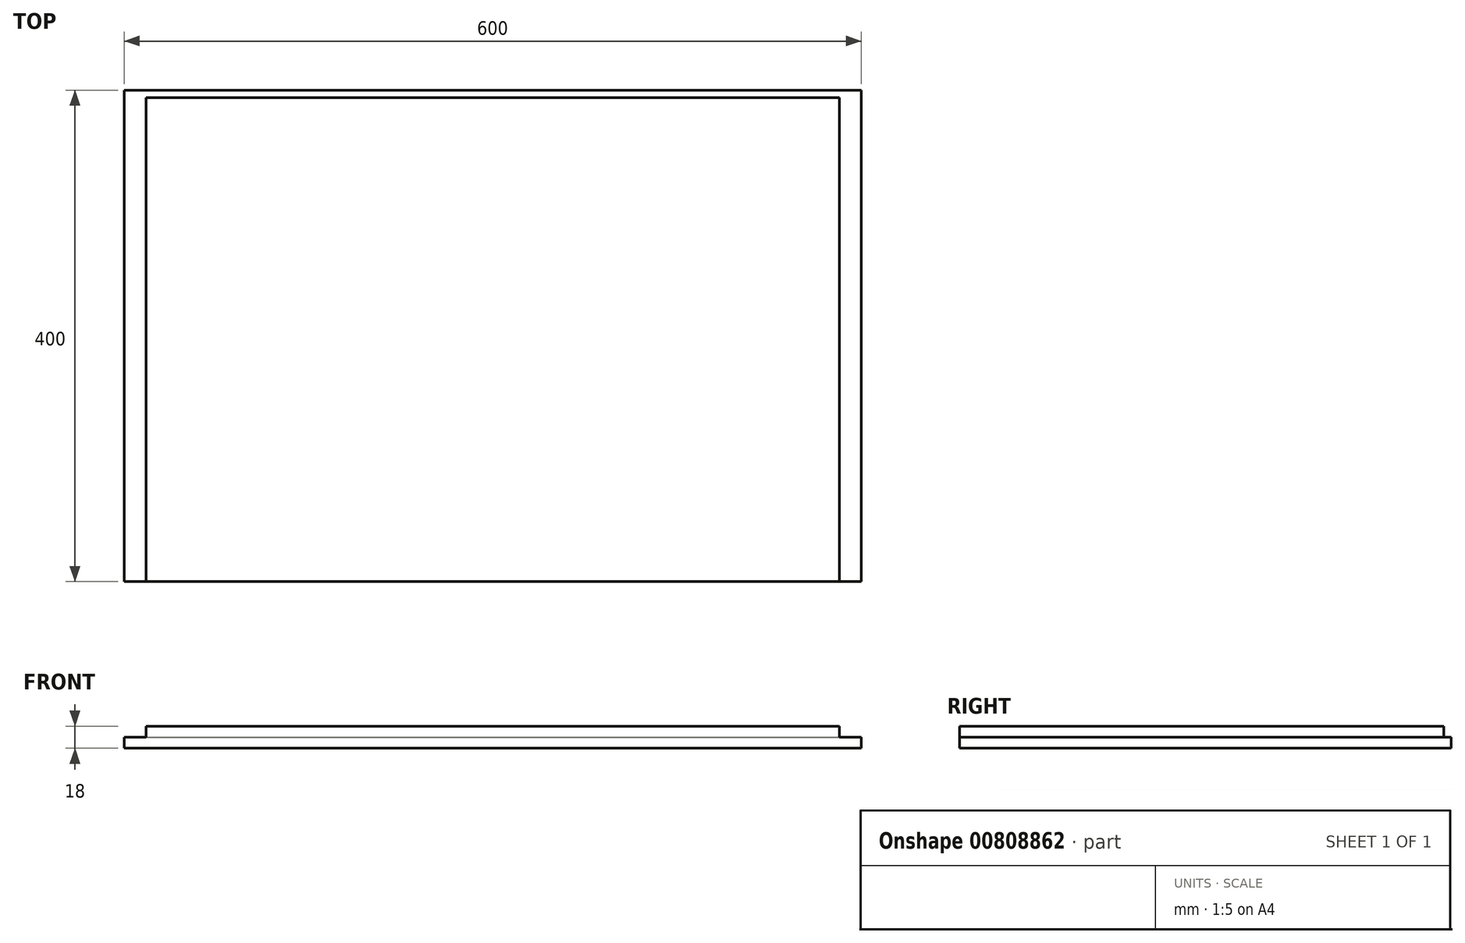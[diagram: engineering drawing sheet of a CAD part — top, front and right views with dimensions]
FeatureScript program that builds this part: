
annotation { "Feature Type Name" : "Feature", "Feature Type Description" : "" }
export const myFeature = defineFeature(function(context is Context, id is Id, definition is map)
    precondition{}
    {
        {
            var Q0;
            Q0=qCreatedBy(makeId("Top.planeOp"),FACE);
            var sketch = newSketch(context, id + "F0", { "sketchPlane" : qUnion([Q0])});
            skLineSegment(sketch, "E0.bottom", {"start": v(0, 0) * mm, "end": v(600, 0) * mm});
            skLineSegment(sketch, "E0.top", {"start": v(0, 400) * mm, "end": v(600, 400) * mm});
            skLineSegment(sketch, "E0.left", {"start": v(0, 0) * mm, "end": v(0, 400) * mm});
            skLineSegment(sketch, "E0.right", {"start": v(600, 0) * mm, "end": v(600, 400) * mm});
            skLineSegment(sketch, "E1.bottom", {"start": v(0, 400) * mm, "end": v(18, 400) * mm});
            skLineSegment(sketch, "E1.top", {"start": v(0, 0) * mm, "end": v(18, 0) * mm});
            skLineSegment(sketch, "E1.left", {"start": v(0, 400) * mm, "end": v(0, 0) * mm});
            skLineSegment(sketch, "E1.right", {"start": v(18, 400) * mm, "end": v(18, 0) * mm});
            skLineSegment(sketch, "E2.bottom", {"start": v(600, 400) * mm, "end": v(582, 400) * mm});
            skLineSegment(sketch, "E2.top", {"start": v(600, 0) * mm, "end": v(582, 0) * mm});
            skLineSegment(sketch, "E2.left", {"start": v(600, 400) * mm, "end": v(600, 0) * mm});
            skLineSegment(sketch, "E2.right", {"start": v(582, 400) * mm, "end": v(582, 0) * mm});
            skLineSegment(sketch, "E3.top", {"start": v(0, 394) * mm, "end": v(600, 394) * mm});
            skLineSegment(sketch, "E3.left", {"start": v(0, 400) * mm, "end": v(0, 394) * mm});
            skLineSegment(sketch, "E3.right", {"start": v(600, 400) * mm, "end": v(600, 394) * mm});
            skSolve(sketch);
        }
        {
            var Q0;
            {var subQ0=sQuery(id+"F0.wireOp",EDGE,"E1.right");var subQ1=sQuery(id+"F0.wireOp",EDGE,"E0.bottom");var subQ2=makeQuery(id+"F0.imprint","INTERSECT",VERTEX,{"derivedFrom":[subQ1,subQ0]});Q0=makeQuery(id+"F0.imprint","IMPRINT",FACE,{"disambiguationData":[TD([[makeQuery(id+"F0.imprint","IMPRINT",EDGE,{"disambiguationData":[TD([[subQ2,-1.0]])],"derivedFrom":subQ1}),1.0]])]});}
            extrude(context, id + "F1", {"entities" : qUnion([Q0]), "depth" : 18 * mm, "offsetDistance" : 25 * mm});
        }
        {
            var Q0;
            {var subQ0=sQuery(id+"F0.wireOp",EDGE,"E1.right");var subQ1=sQuery(id+"F0.wireOp",EDGE,"E0.bottom");var subQ2=makeQuery(id+"F0.imprint","INTERSECT",VERTEX,{"derivedFrom":[subQ1,subQ0]});Q0=makeQuery(id+"F0.imprint","IMPRINT",FACE,{"disambiguationData":[TD([[makeQuery(id+"F0.imprint","IMPRINT",EDGE,{"disambiguationData":[TD([[subQ2,1.0]])],"derivedFrom":subQ1}),1.0]])]});}
            var Q1;
            {var subQ0=sQuery(id+"F0.wireOp",EDGE,"E1.right");var subQ1=sQuery(id+"F0.wireOp",EDGE,"E0.top");var subQ2=makeQuery(id+"F0.imprint","INTERSECT",VERTEX,{"derivedFrom":[subQ1,subQ0]});Q1=makeQuery(id+"F0.imprint","IMPRINT",FACE,{"disambiguationData":[TD([[makeQuery(id+"F0.imprint","IMPRINT",EDGE,{"disambiguationData":[TD([[subQ2,-1.0]])],"derivedFrom":subQ1}),-1.0]])]});}
            var Q2;
            {var subQ0=sQuery(id+"F0.wireOp",EDGE,"E1.right");var subQ1=sQuery(id+"F0.wireOp",EDGE,"E0.top");var subQ2=makeQuery(id+"F0.imprint","INTERSECT",VERTEX,{"derivedFrom":[subQ1,subQ0]});Q2=makeQuery(id+"F0.imprint","IMPRINT",FACE,{"disambiguationData":[TD([[makeQuery(id+"F0.imprint","IMPRINT",EDGE,{"disambiguationData":[TD([[subQ2,1.0]])],"derivedFrom":subQ1}),-1.0]])]});}
            var Q3;
            {var subQ0=sQuery(id+"F0.wireOp",EDGE,"E0.right");var subQ1=sQuery(id+"F0.wireOp",EDGE,"E0.top");var subQ2=makeQuery(id+"F0.imprint","INTERSECT",VERTEX,{"derivedFrom":[subQ1,subQ0]});Q3=makeQuery(id+"F0.imprint","IMPRINT",FACE,{"disambiguationData":[TD([[makeQuery(id+"F0.imprint","IMPRINT",EDGE,{"disambiguationData":[TD([[subQ2,1.0]])],"derivedFrom":subQ1}),-1.0]])]});}
            var Q4;
            {var subQ0=sQuery(id+"F0.wireOp",EDGE,"E0.right");var subQ1=sQuery(id+"F0.wireOp",EDGE,"E0.bottom");var subQ2=makeQuery(id+"F0.imprint","INTERSECT",VERTEX,{"derivedFrom":[subQ1,subQ0]});Q4=makeQuery(id+"F0.imprint","IMPRINT",FACE,{"disambiguationData":[TD([[makeQuery(id+"F0.imprint","IMPRINT",EDGE,{"disambiguationData":[TD([[subQ2,1.0]])],"derivedFrom":subQ1}),1.0]])]});}
            extrude(context, id + "F2", {"entities" : qUnion([Q0, Q1, Q2, Q3, Q4]), "operationType" : NewBodyOperationType.ADD, "depth" : 9 * mm, "offsetDistance" : 25 * mm});
        }
    });
